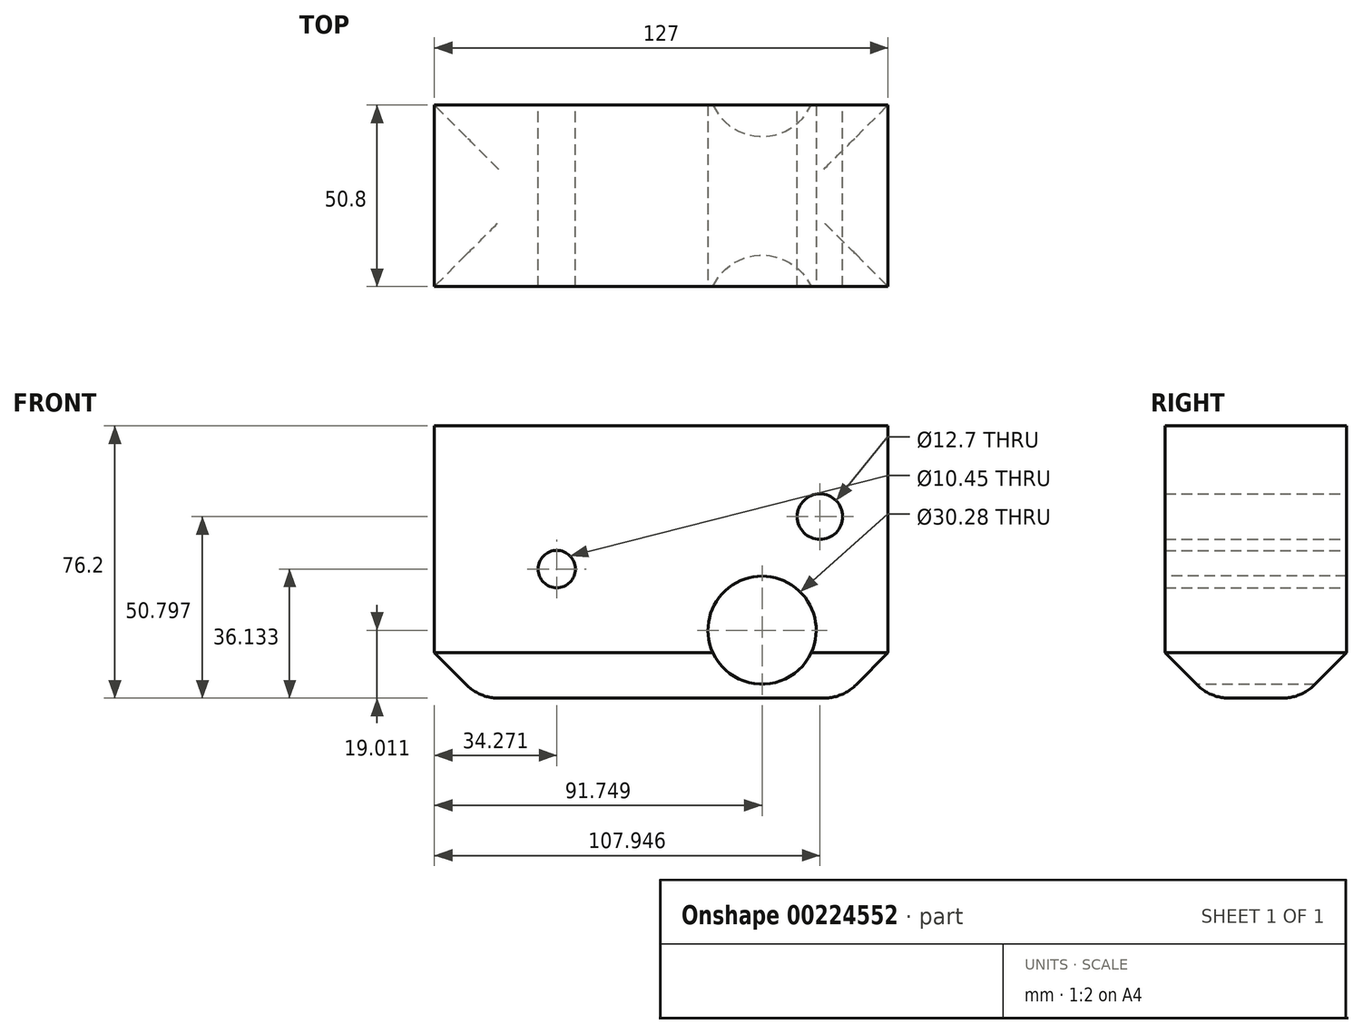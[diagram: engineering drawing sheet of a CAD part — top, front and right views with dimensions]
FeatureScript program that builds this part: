
annotation { "Feature Type Name" : "Feature", "Feature Type Description" : "" }
export const myFeature = defineFeature(function(context is Context, id is Id, definition is map)
    precondition{}
    {
        {
            var Q0;
            Q0=qCreatedBy(makeId("Front.planeOp"),FACE);
            var sketch = newSketch(context, id + "F0", { "sketchPlane" : qUnion([Q0])});
            skLineSegment(sketch, "E0.bottom", {"start": v(-65.15, -28.71) * mm, "end": v(61.85, -28.71) * mm});
            skLineSegment(sketch, "E0.top", {"start": v(-65.15, -104.91) * mm, "end": v(61.85, -104.91) * mm});
            skLineSegment(sketch, "E0.left", {"start": v(-65.15, -28.71) * mm, "end": v(-65.15, -104.91) * mm});
            skLineSegment(sketch, "E0.right", {"start": v(61.85, -28.71) * mm, "end": v(61.85, -104.91) * mm});
            skCircle(sketch, "E1", {"center": v(42.8, -54.11) * mm, "radius": 6.35 * mm});
            skCircle(sketch, "E2", {"center": v(-30.88, -68.78) * mm, "radius": 5.22 * mm});
            skSolve(sketch);
        }
        {
            var Q0;
            Q0=makeQuery(id+"F0.imprint","IMPRINT",FACE,{"disambiguationData":[TD([[makeQuery(id+"F0.imprint","IMPRINT",EDGE,{"derivedFrom":sQuery(id+"F0.wireOp",EDGE,"E0.bottom")}),-1.0]])]});
            extrude(context, id + "F1", {"entities" : qUnion([Q0]), "depth" : 50.8 * mm});
        }
        {
            var Q0;
            Q0=makeQuery(id+"F1.opExtrude","CAP_FACE",FACE,{"disambiguationData":[OSD([sQuery(id+"F0.wireOp",EDGE,"E0.bottom"),sQuery(id+"F0.wireOp",EDGE,"E0.top"),sQuery(id+"F0.wireOp",EDGE,"E0.left"),sQuery(id+"F0.wireOp",EDGE,"E0.right"),sQuery(id+"F0.wireOp",EDGE,"E1"),sQuery(id+"F0.wireOp",EDGE,"E2")])],"isStart":false});
            var sketch = newSketch(context, id + "F2", { "sketchPlane" : qUnion([Q0])});
            skCircle(sketch, "E3", {"center": v(26.6, -85.9) * mm, "radius": 15.14 * mm});
            skSolve(sketch);
        }
        {
            var Q0;
            Q0=makeQuery(id+"F2.imprint","IMPRINT",FACE,{"disambiguationData":[TD([[makeQuery(id+"F2.imprint","IMPRINT",EDGE,{"derivedFrom":sQuery(id+"F2.wireOp",EDGE,"E3")}),1.0]])]});
            extrude(context, id + "F3", {"entities" : qUnion([Q0]), "operationType" : NewBodyOperationType.REMOVE, "oppositeDirection" : true, "depth" : 138.94 * mm});
        }
        {
            var Q0;
            Q0=makeQuery(id+"F1.opExtrude","SWEPT_EDGE",EDGE,{"disambiguationData":[OSD([sQuery(id+"F0.wireOp",EDGE,"E0.top"),sQuery(id+"F0.wireOp",EDGE,"E0.right")])]});
            var Q1;
            Q1=makeQuery(id+"F1.opExtrude","SWEPT_EDGE",EDGE,{"disambiguationData":[OSD([sQuery(id+"F0.wireOp",EDGE,"E0.top"),sQuery(id+"F0.wireOp",EDGE,"E0.left")])]});
            var Q2;
            Q2=makeQuery(id+"F1.opExtrude","CAP_EDGE",EDGE,{"disambiguationData":[OSD([sQuery(id+"F0.wireOp",EDGE,"E0.top")])],"isStart":false});
            var Q3;
            Q3=makeQuery(id+"F1.opExtrude","CAP_EDGE",EDGE,{"disambiguationData":[OSD([sQuery(id+"F0.wireOp",EDGE,"E0.top")])],"isStart":true});
            chamfer(context, id + "F4", {"entities" : qUnion([Q0, Q1, Q2, Q3]), "width" : 12.7 * mm, "tangentPropagation" : true});
        }
        {
            var Q0;
            {var subQ0=sQuery(id+"F0.wireOp",EDGE,"E0.top");Q0=makeQuery(id+"F4.opChamfer","BLEND_EDGE",EDGE,{"blendedFrom":[makeQuery(id+"F1.opExtrude","CAP_EDGE",EDGE,{"disambiguationData":[OSD([subQ0])],"isStart":false}),makeQuery(id+"F1.opExtrude","SWEPT_FACE",FACE,{"disambiguationData":[OSD([subQ0])]})],"blendedInto":[makeQuery(id+"F1.opExtrude","SWEPT_FACE",FACE,{"disambiguationData":[OSD([subQ0])]})]});}
            var Q1;
            {var subQ0=sQuery(id+"F0.wireOp",EDGE,"E0.top");Q1=makeQuery(id+"F4.opChamfer","BLEND_EDGE",EDGE,{"blendedFrom":[makeQuery(id+"F1.opExtrude","CAP_EDGE",EDGE,{"disambiguationData":[OSD([subQ0])],"isStart":true}),makeQuery(id+"F1.opExtrude","SWEPT_FACE",FACE,{"disambiguationData":[OSD([subQ0])]})],"blendedInto":[makeQuery(id+"F1.opExtrude","SWEPT_FACE",FACE,{"disambiguationData":[OSD([subQ0])]})]});}
            var Q2;
            {var subQ0=sQuery(id+"F0.wireOp",EDGE,"E0.top");Q2=makeQuery(id+"F4.opChamfer","BLEND_EDGE",EDGE,{"blendedFrom":[makeQuery(id+"F1.opExtrude","SWEPT_EDGE",EDGE,{"disambiguationData":[OSD([subQ0,sQuery(id+"F0.wireOp",EDGE,"E0.right")])]}),makeQuery(id+"F1.opExtrude","SWEPT_FACE",FACE,{"disambiguationData":[OSD([subQ0])]})],"blendedInto":[makeQuery(id+"F1.opExtrude","SWEPT_FACE",FACE,{"disambiguationData":[OSD([subQ0])]})]});}
            var Q3;
            {var subQ0=sQuery(id+"F0.wireOp",EDGE,"E0.top");Q3=makeQuery(id+"F4.opChamfer","BLEND_EDGE",EDGE,{"blendedFrom":[makeQuery(id+"F1.opExtrude","SWEPT_EDGE",EDGE,{"disambiguationData":[OSD([subQ0,sQuery(id+"F0.wireOp",EDGE,"E0.left")])]}),makeQuery(id+"F1.opExtrude","SWEPT_FACE",FACE,{"disambiguationData":[OSD([subQ0])]})],"blendedInto":[makeQuery(id+"F1.opExtrude","SWEPT_FACE",FACE,{"disambiguationData":[OSD([subQ0])]})]});}
            fillet(context, id + "F5", {"entities" : qUnion([Q0, Q1, Q2, Q3]), "radius" : 12.7 * mm, "tangentPropagation" : true, "allowEdgeOverflow" : false});
        }
    });
